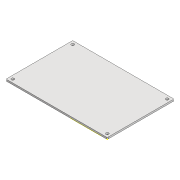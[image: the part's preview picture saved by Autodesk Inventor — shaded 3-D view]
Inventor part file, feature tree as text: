
AUTODESK INVENTOR PART (.ipt)
format: ipt  version: 2020 (Build 240168000, 168)  size: 148,480 bytes
history: native  units: mm
features: other x32, extrude x4, sketch x4, fillet x1
ambient origin geometry x8: Origin, YZ Plane, XZ Plane, XY Plane, X Axis, Y Axis, Z Axis, Center Point
bodies: Body1 (feature_tree)
feature tree (41):
  other  "Sólido1"
  extrude  "Extrusão1"  Depth=158.0mm
  fillet  "Arredondamento1"  Radius=4.0mm
  extrude  "Extrusão2"  Depth=2.0mm
  extrude  "Extrusão3"  Depth=6.7mm
  extrude  "Extrusão4"  Depth=10.0mm
  sketch  "Esboço1"  dims[d0=252.0mm d1=158.0mm d2=4.0mm d3=0.0mm]
  sketch  "Esboço2"  dims[d4=2.0mm d5=6.7mm]
  sketch  "Esboço3"  dims[d6=6.7mm d7=6.7mm]
  other  "Referência1"
  other  "Referência2"
  other  "Referência3"
  other  "Referência4"
  other  "Referência5"
  other  "Referência6"
  other  "Referência7"
  other  "Referência8"
  other  "Referência9"
  other  "Referência10"
  other  "Referência11"
  other  "Referência12"
  other  "Referência13"
  other  "Referência14"
  sketch  "Esboço4"  dims[d8=6.7mm d9=8.0mm d10=8.0mm d11=8.0mm d12=8.0mm d13=8.0mm d14=8.0mm d15=8.0mm d16=8.0mm d17=10.0mm d18=0.0mm d19=10.0mm d20=0.0mm d21=10.0mm d22=0.0mm]
  other  "Referência15"
  other  "Referência16"
  other  "Referência17"
  other  "Referência18"
  other  "Referência19"
  other  "Referência20"
  other  "Referência21"
  other  "Referência22"
  other  "<userpath>\OneDrive\Área de Trabalho\Calorimetro 2022\Inventor\Calorímetro.iam"
  other  "Calorímetro.iam"
  other  "ATX Power Supply v1:1"
  other  "Cover:1"
  other  "suporte-fonte:1"
  other  "suporte_fechamento:2"
  other  "suporte_fechamento2:3"
  other  "suporte_fechamento:1"
  other  "suporte_fechamento2:2"
